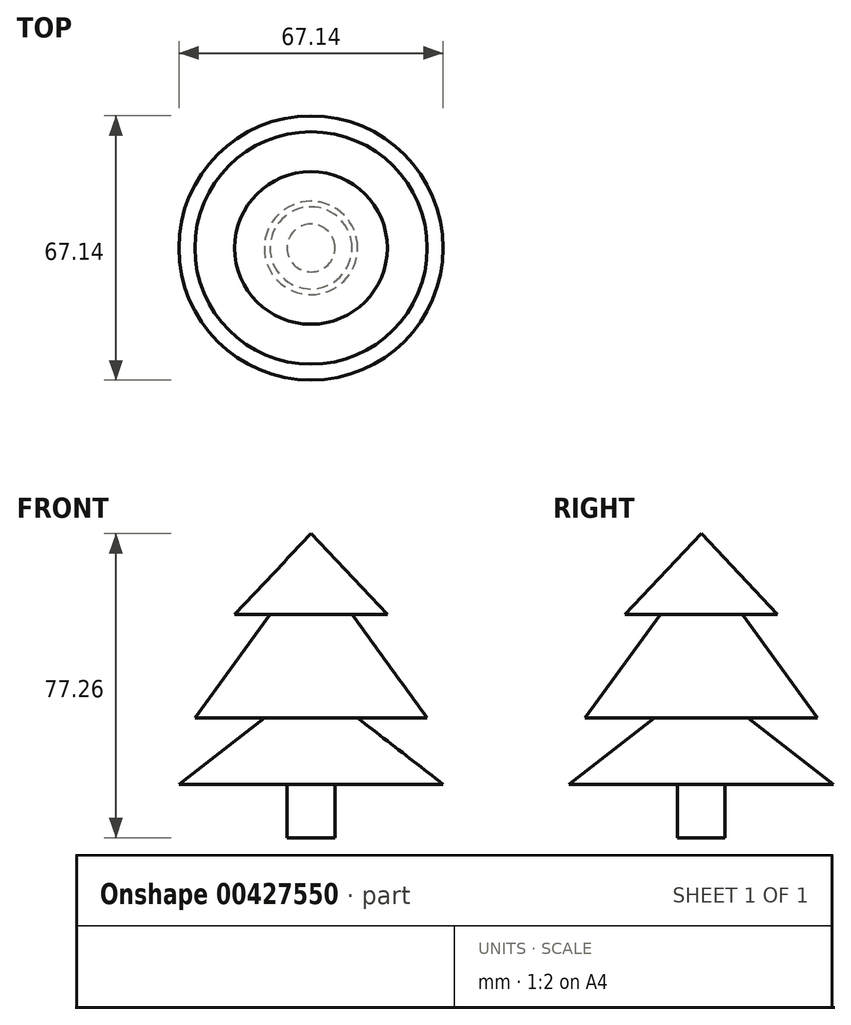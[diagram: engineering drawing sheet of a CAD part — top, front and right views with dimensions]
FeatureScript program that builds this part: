
annotation { "Feature Type Name" : "Feature", "Feature Type Description" : "" }
export const myFeature = defineFeature(function(context is Context, id is Id, definition is map)
    precondition{}
    {
        {
            var Q0;
            Q0=qCreatedBy(makeId("Front.planeOp"),FACE);
            var sketch = newSketch(context, id + "F0", { "sketchPlane" : qUnion([Q0])});
            skLineSegment(sketch, "E0", {"start": v(0, 34.87) * mm, "end": v(-19.39, 14.32) * mm});
            skLineSegment(sketch, "E1", {"start": v(-19.39, 14.32) * mm, "end": v(-10.42, 14.32) * mm});
            skLineSegment(sketch, "E2", {"start": v(-10.42, 14.32) * mm, "end": v(-29.52, -12) * mm});
            skLineSegment(sketch, "E3", {"start": v(-29.52, -12) * mm, "end": v(-11.86, -12) * mm});
            skLineSegment(sketch, "E4", {"start": v(-11.86, -12) * mm, "end": v(-33.57, -28.8) * mm});
            skLineSegment(sketch, "E5", {"start": v(-33.57, -28.8) * mm, "end": v(-6.08, -28.8) * mm});
            skLineSegment(sketch, "E6", {"start": v(-6.08, -28.8) * mm, "end": v(-6.08, -42.4) * mm});
            skLineSegment(sketch, "E7", {"start": v(-6.08, -42.4) * mm, "end": v(0, -42.4) * mm});
            skLineSegment(sketch, "E8", {"start": v(0, 34.87) * mm, "end": v(0, -42.4) * mm});
            skSolve(sketch);
        }
        {
            var Q0;
            Q0 = qSketchRegion(id + "F0", true);
            var Q1;
            Q1=sQuery(id+"F0.wireOp",EDGE,"E8");
            revolve(context, id + "F1", {"entities" : qUnion([Q0]), "axis" : qUnion([Q1]), "revolveType" : RevolveType.FULL});
        }
    });
